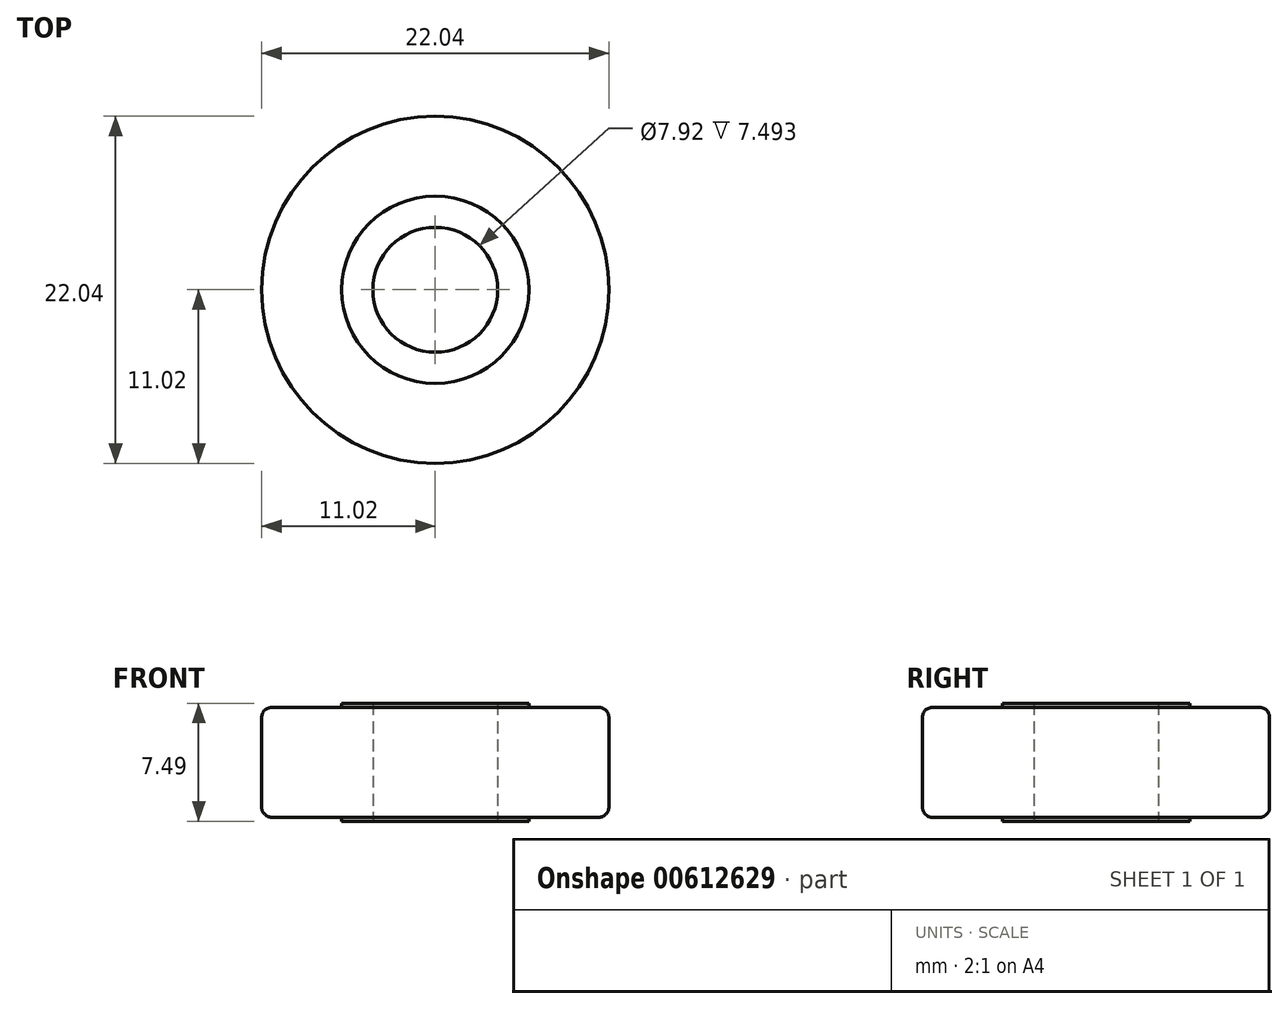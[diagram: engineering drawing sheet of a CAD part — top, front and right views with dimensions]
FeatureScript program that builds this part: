
annotation { "Feature Type Name" : "Feature", "Feature Type Description" : "" }
export const myFeature = defineFeature(function(context is Context, id is Id, definition is map)
    precondition{}
    {
        {
            var Q0;
            Q0=qCreatedBy(makeId("Top.planeOp"),FACE);
            var sketch = newSketch(context, id + "F0", { "sketchPlane" : qUnion([Q0])});
            skCircle(sketch, "E0", {"center": v(0, 0) * mm, "radius": 11.02 * mm});
            skCircle(sketch, "E1", {"center": v(0, 0) * mm, "radius": 3.96 * mm});
            skCircle(sketch, "E2", {"center": v(0, 0) * mm, "radius": 5.84 * mm});
            skSolve(sketch);
        }
        {
            var Q0;
            Q0=makeQuery(id+"F0.imprint","IMPRINT",FACE,{"disambiguationData":[TD([[makeQuery(id+"F0.imprint","IMPRINT",EDGE,{"derivedFrom":sQuery(id+"F0.wireOp",EDGE,"E0")}),1.0]])]});
            var Q1;
            Q1=makeQuery(id+"F0.imprint","IMPRINT",FACE,{"disambiguationData":[TD([[makeQuery(id+"F0.imprint","IMPRINT",EDGE,{"derivedFrom":sQuery(id+"F0.wireOp",EDGE,"E1")}),-1.0]])]});
            extrude(context, id + "F1", {"entities" : qUnion([Q0, Q1]), "depth" : 7 * mm, "offsetDistance" : 25.4 * mm});
        }
        {
            var Q0;
            Q0=makeQuery(id+"F1.opExtrude","CAP_EDGE",EDGE,{"disambiguationData":[OSD([sQuery(id+"F0.wireOp",EDGE,"E0")])],"isStart":true});
            var Q1;
            Q1=makeQuery(id+"F1.opExtrude","CAP_EDGE",EDGE,{"disambiguationData":[OSD([sQuery(id+"F0.wireOp",EDGE,"E0")])],"isStart":false});
            fillet(context, id + "F2", {"entities" : qUnion([Q0, Q1]), "radius" : 0.64 * mm, "tangentPropagation" : true, "allowEdgeOverflow" : false});
        }
        {
            var Q0;
            Q0=makeQuery(id+"F1.opExtrude","CAP_FACE",FACE,{"disambiguationData":[OSD([sQuery(id+"F0.wireOp",EDGE,"E0"),sQuery(id+"F0.wireOp",EDGE,"E1")])],"isStart":false});
            var sketch = newSketch(context, id + "F3", { "sketchPlane" : qUnion([Q0])});
            skCircle(sketch, "E3", {"center": v(0, 0) * mm, "radius": 5.94 * mm});
            skSolve(sketch);
        }
        {
            var Q0;
            Q0=makeQuery(id+"F3.imprint","IMPRINT",FACE,{"disambiguationData":[TD([[makeQuery(id+"F3.imprint","IMPRINT",EDGE,{"derivedFrom":sQuery(id+"F3.wireOp",EDGE,"E3")}),1.0]])]});
            extrude(context, id + "F4", {"entities" : qUnion([Q0]), "operationType" : NewBodyOperationType.ADD, "depth" : 0.25 * mm, "offsetDistance" : 25.4 * mm, "hasSecondDirection" : true, "secondDirectionOppositeDirection" : true, "secondDirectionDepth" : 7.24 * mm});
        }
    });
